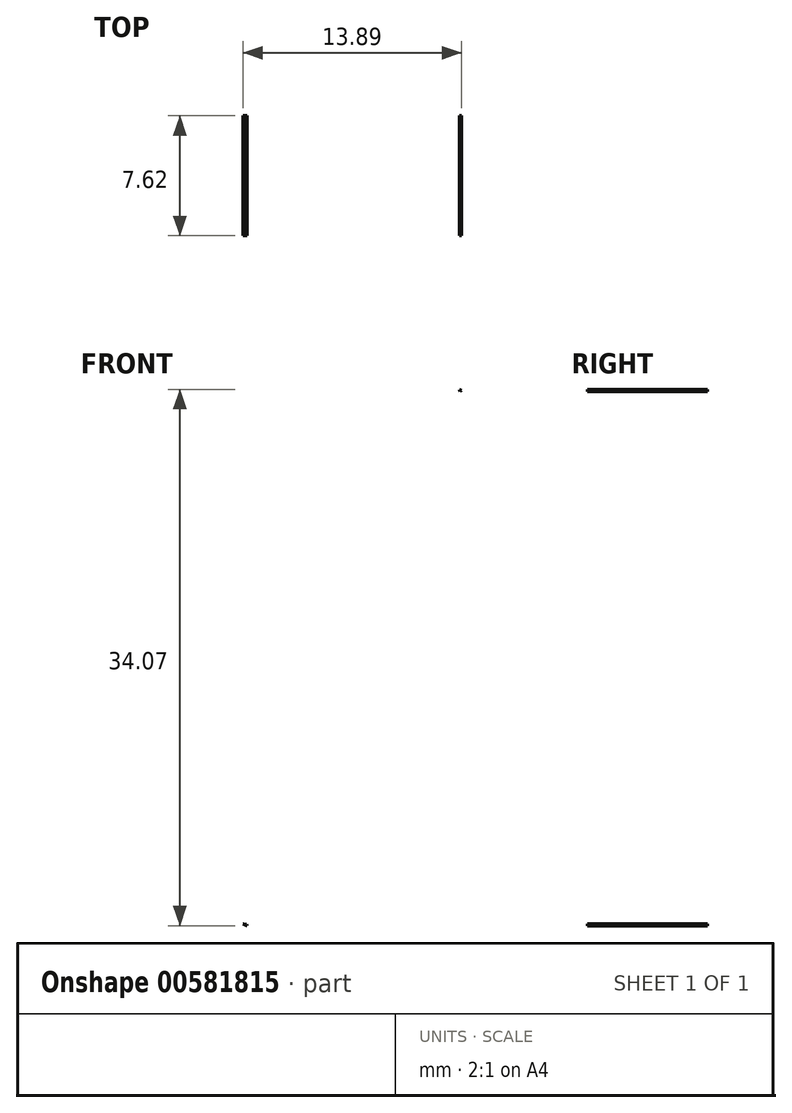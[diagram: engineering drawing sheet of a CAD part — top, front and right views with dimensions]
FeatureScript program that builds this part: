
annotation { "Feature Type Name" : "Feature", "Feature Type Description" : "" }
export const myFeature = defineFeature(function(context is Context, id is Id, definition is map)
    precondition{}
    {
        {
            var Q0;
            Q0=qCreatedBy(makeId("Front.planeOp"),FACE);
            var sketch = newSketch(context, id + "F0", { "sketchPlane" : qUnion([Q0])});
            skLineSegment(sketch, "E0", {"start": v(-52.43, 28.32) * mm, "end": v(-34.99, 41.22) * mm});
            skLineSegment(sketch, "E1", {"start": v(-34.99, 41.22) * mm, "end": v(0, 18.11) * mm});
            skLineSegment(sketch, "E2.MirrorCS", {"start": v(34.99, 41.22) * mm, "end": v(0, 18.11) * mm});
            skLineSegment(sketch, "E3", {"start": v(34.99, 41.22) * mm, "end": v(52.43, 28.32) * mm});
            skLineSegment(sketch, "E4", {"start": v(-52.43, 28.32) * mm, "end": v(-54.84, 6.63) * mm});
            skLineSegment(sketch, "E5.MirrorCS", {"start": v(52.43, 28.32) * mm, "end": v(54.84, 6.63) * mm});
            skLineSegment(sketch, "E6", {"start": v(-54.84, 6.63) * mm, "end": v(-16.04, -8.41) * mm});
            skLineSegment(sketch, "E7.MirrorCS", {"start": v(54.84, 6.63) * mm, "end": v(16.04, -8.41) * mm});
            skLineSegment(sketch, "E8", {"start": v(0, -58.56) * mm, "end": v(19.94, -50.02) * mm});
            skLineSegment(sketch, "E9", {"start": v(19.94, -50.02) * mm, "end": v(16.04, -8.41) * mm});
            skLineSegment(sketch, "E10", {"start": v(0, -58.56) * mm, "end": v(-19.94, -50.02) * mm});
            skLineSegment(sketch, "E11", {"start": v(-19.94, -50.02) * mm, "end": v(-16.04, -8.41) * mm});
            skSolve(sketch);
        }
        {
            var Q0;
            Q0 = qSketchRegion(id + "F0", true);
            extrude(context, id + "F1", {"entities" : qUnion([Q0]), "depth" : 7.62 * mm, "offsetDistance" : 25.4 * mm});
        }
        {
            var Q0;
            Q0=qCreatedBy(makeId("Front.planeOp"),FACE);
            var sketch = newSketch(context, id + "F2", { "sketchPlane" : qUnion([Q0])});
            skCircle(sketch, "E12", {"center": v(0, 0) * mm, "radius": 11 * mm});
            skCircle(sketch, "E13", {"center": v(-33.24, 17) * mm, "radius": 11 * mm});
            skCircle(sketch, "E14", {"center": v(33.05, 17.38) * mm, "radius": 11 * mm});
            skCircle(sketch, "E15", {"center": v(0, -37.34) * mm, "radius": 11 * mm});
            skSolve(sketch);
        }
        {
            var Q0;
            Q0 = qSketchRegion(id + "F2", true);
            extrude(context, id + "F3", {"entities" : qUnion([Q0]), "operationType" : NewBodyOperationType.REMOVE, "endBound" : BoundingType.THROUGH_ALL, "depth" : 25.4 * mm, "offsetDistance" : 25.4 * mm});
        }
        {
            var Q0;
            Q0=qCreatedBy(makeId("Front.planeOp"),FACE);
            var sketch = newSketch(context, id + "F4", { "sketchPlane" : qUnion([Q0])});
            skLineSegment(sketch, "E16", {"start": v(-41.96, 38.65) * mm, "end": v(-26.02, 38.65) * mm});
            skLineSegment(sketch, "E17", {"start": v(-26.02, 38.65) * mm, "end": v(-26.02, 43.76) * mm});
            skLineSegment(sketch, "E18", {"start": v(-26.02, 43.76) * mm, "end": v(-40.46, 43.76) * mm});
            skLineSegment(sketch, "E19", {"start": v(-40.46, 43.76) * mm, "end": v(-41.96, 38.65) * mm});
            skLineSegment(sketch, "E20.MirrorCS", {"start": v(26.02, 43.76) * mm, "end": v(40.46, 43.76) * mm});
            skLineSegment(sketch, "E21.MirrorCS", {"start": v(26.02, 38.65) * mm, "end": v(26.02, 43.76) * mm});
            skLineSegment(sketch, "E22.MirrorCS", {"start": v(41.96, 38.65) * mm, "end": v(26.02, 38.65) * mm});
            skLineSegment(sketch, "E23.MirrorCS", {"start": v(40.46, 43.76) * mm, "end": v(41.96, 38.65) * mm});
            skLineSegment(sketch, "E24", {"start": v(-55.8, 12.48) * mm, "end": v(-47.37, 0) * mm});
            skLineSegment(sketch, "E25", {"start": v(-47.37, 0) * mm, "end": v(-58.2, 0) * mm});
            skLineSegment(sketch, "E26", {"start": v(-58.2, 0) * mm, "end": v(-55.8, 12.48) * mm});
            skLineSegment(sketch, "E27.MirrorCS", {"start": v(55.8, 12.48) * mm, "end": v(47.37, 0) * mm});
            skLineSegment(sketch, "E28.MirrorCS", {"start": v(58.2, 0) * mm, "end": v(55.8, 12.48) * mm});
            skLineSegment(sketch, "E29.MirrorCS", {"start": v(47.37, 0) * mm, "end": v(58.2, 0) * mm});
            skLineSegment(sketch, "E30", {"start": v(-20.6, -44.37) * mm, "end": v(-13.08, -56.1) * mm});
            skLineSegment(sketch, "E31", {"start": v(-13.08, -56.1) * mm, "end": v(-22.1, -56.1) * mm});
            skLineSegment(sketch, "E32", {"start": v(-22.1, -56.1) * mm, "end": v(-20.6, -44.37) * mm});
            skLineSegment(sketch, "E33.MirrorCS", {"start": v(20.6, -44.37) * mm, "end": v(13.08, -56.1) * mm});
            skLineSegment(sketch, "E34.MirrorCS", {"start": v(22.1, -56.1) * mm, "end": v(20.6, -44.37) * mm});
            skLineSegment(sketch, "E35.MirrorCS", {"start": v(13.08, -56.1) * mm, "end": v(22.1, -56.1) * mm});
            skSolve(sketch);
        }
        {
            var Q0;
            Q0 = qSketchRegion(id + "F4", true);
            extrude(context, id + "F5", {"entities" : qUnion([Q0]), "operationType" : NewBodyOperationType.REMOVE, "endBound" : BoundingType.THROUGH_ALL, "depth" : 25.4 * mm, "offsetDistance" : 25.4 * mm});
        }
        {
            var Q0;
            Q0=qCreatedBy(makeId("Front.planeOp"),FACE);
            var sketch = newSketch(context, id + "F6", { "sketchPlane" : qUnion([Q0])});
            skFitSpline(sketch, "E36", {"points": [v(-49.78, 26.92) * mm, v(-44.37, 33.24) * mm, v(-36.85, 36.25) * mm, v(-29.63, 36.25) * mm, v(-24.03, 33.84) * mm, v(-17.6, 27.52) * mm, v(-10.68, 18.2) * mm, v(-4.66, 14.59) * mm, v(0, 13.99) * mm, v(4.96, 14.29) * mm, v(10.68, 17.9) * mm, v(18.2, 27.22) * mm, v(23.91, 34.14) * mm, v(30.23, 36.85) * mm, v(37.75, 36.85) * mm, v(44.97, 32.64) * mm, v(49.78, 26.92) * mm, v(52.49, 19.7) * mm, v(52.49, 11.58) * mm, v(48.88, 5.26) * mm, v(44.97, 2.56) * mm, v(32.03, 0) * mm, v(19.4, -2.26) * mm, v(13.69, -5.26) * mm, v(11.28, -10.38) * mm, v(12.18, -19.1) * mm, v(15.67, -27.22) * mm, v(18.98, -36.85) * mm, v(16.1, -48.88) * mm, v(8.57, -54.6) * mm, v(0, -56.7) * mm, v(-8.27, -54.6) * mm, v(-14.7, -49.78) * mm, v(-18.92, -38.95) * mm, v(-15.6, -25.72) * mm, v(-13.08, -21.5) * mm, v(-13.08, -21.5) * mm, v(-10.68, -15.8) * mm, v(-10.38, -10.08) * mm, v(-15.3, -2.26) * mm, v(-28.84, 0) * mm, v(-37.57, 0) * mm, v(-49.6, 7.07) * mm, v(-52.6, 18.8) * mm, v(-49.78, 26.92) * mm]});
            skLineSegment(sketch, "E37", {"start": v(-24.03, 33.84) * mm, "end": v(9.35, 52.72) * mm});
            skLineSegment(sketch, "E38", {"start": v(9.35, 52.72) * mm, "end": v(23.91, 34.14) * mm});
            skLineSegment(sketch, "E39", {"start": v(-37.57, 0) * mm, "end": v(-18.92, -38.95) * mm});
            skLineSegment(sketch, "E40", {"start": v(18.98, -36.85) * mm, "end": v(44.97, 2.56) * mm});
            skLineSegment(sketch, "E41", {"start": v(-37.57, 0) * mm, "end": v(-62.53, 2.56) * mm});
            skLineSegment(sketch, "E42", {"start": v(-62.53, 2.56) * mm, "end": v(-62.53, 40.46) * mm});
            skLineSegment(sketch, "E43", {"start": v(-62.53, 40.46) * mm, "end": v(-25.53, 49.48) * mm});
            skLineSegment(sketch, "E44", {"start": v(-25.53, 49.48) * mm, "end": v(-24.03, 33.84) * mm});
            skLineSegment(sketch, "E45", {"start": v(23.91, 34.14) * mm, "end": v(37.93, 60.6) * mm});
            skLineSegment(sketch, "E46", {"start": v(37.93, 60.6) * mm, "end": v(59.6, 49.13) * mm});
            skLineSegment(sketch, "E47", {"start": v(59.6, 49.13) * mm, "end": v(65.9, 25.42) * mm});
            skLineSegment(sketch, "E48", {"start": v(65.9, 25.42) * mm, "end": v(57.48, -5.56) * mm});
            skLineSegment(sketch, "E49", {"start": v(57.48, -5.56) * mm, "end": v(44.97, 2.56) * mm});
            skLineSegment(sketch, "E50", {"start": v(18.98, -36.85) * mm, "end": v(30.41, -52.79) * mm});
            skLineSegment(sketch, "E51", {"start": v(30.41, -52.79) * mm, "end": v(0, -70) * mm});
            skLineSegment(sketch, "E52", {"start": v(0, -70) * mm, "end": v(-28.54, -58.5) * mm});
            skLineSegment(sketch, "E53", {"start": v(-28.54, -58.5) * mm, "end": v(-18.92, -38.95) * mm});
            skSolve(sketch);
        }
        {
            var Q0;
            {var subQ0=sQuery(id+"F6.wireOp",EDGE,"E37");Q0=makeQuery(id+"F6.imprint","IMPRINT",FACE,{"disambiguationData":[TD([[makeQuery(id+"F6.imprint","IMPRINT",EDGE,{"derivedFrom":subQ0}),-1.0]])]});}
            var Q1;
            {var subQ0=sQuery(id+"F6.wireOp",EDGE,"E45");Q1=makeQuery(id+"F6.imprint","IMPRINT",FACE,{"disambiguationData":[TD([[makeQuery(id+"F6.imprint","IMPRINT",EDGE,{"derivedFrom":subQ0}),-1.0]])]});}
            var Q2;
            {var subQ0=sQuery(id+"F6.wireOp",EDGE,"E40");Q2=makeQuery(id+"F6.imprint","IMPRINT",FACE,{"disambiguationData":[TD([[makeQuery(id+"F6.imprint","IMPRINT",EDGE,{"derivedFrom":subQ0}),1.0]])]});}
            var Q3;
            {var subQ0=sQuery(id+"F6.wireOp",EDGE,"E50");Q3=makeQuery(id+"F6.imprint","IMPRINT",FACE,{"disambiguationData":[TD([[makeQuery(id+"F6.imprint","IMPRINT",EDGE,{"derivedFrom":subQ0}),-1.0]])]});}
            var Q4;
            {var subQ0=sQuery(id+"F6.wireOp",EDGE,"E39");Q4=makeQuery(id+"F6.imprint","IMPRINT",FACE,{"disambiguationData":[TD([[makeQuery(id+"F6.imprint","IMPRINT",EDGE,{"derivedFrom":subQ0}),1.0]])]});}
            var Q5;
            {var subQ0=sQuery(id+"F6.wireOp",EDGE,"E41");Q5=makeQuery(id+"F6.imprint","IMPRINT",FACE,{"disambiguationData":[TD([[makeQuery(id+"F6.imprint","IMPRINT",EDGE,{"derivedFrom":subQ0}),-1.0]])]});}
            extrude(context, id + "F7", {"entities" : qUnion([Q0, Q1, Q2, Q3, Q4, Q5]), "operationType" : NewBodyOperationType.REMOVE, "endBound" : BoundingType.THROUGH_ALL, "depth" : 25.4 * mm, "offsetDistance" : 25.4 * mm});
        }
        {
            var Q0;
            Q0=qCreatedBy(makeId("Front.planeOp"),FACE);
            var sketch = newSketch(context, id + "F8", { "sketchPlane" : qUnion([Q0])});
            skLineSegment(sketch, "E54", {"start": v(16.28, -23.91) * mm, "end": v(19.28, -36.25) * mm});
            skLineSegment(sketch, "E55", {"start": v(19.28, -36.25) * mm, "end": v(19.28, -30.08) * mm});
            skPoint(sketch, "E55.endSnap0", {"position": v(17.78, -30.08) * mm});
            skLineSegment(sketch, "E56", {"start": v(19.28, -30.08) * mm, "end": v(16.28, -23.91) * mm});
            skSolve(sketch);
        }
        {
            var Q0;
            Q0 = qSketchRegion(id + "F8", true);
            extrude(context, id + "F9", {"entities" : qUnion([Q0]), "operationType" : NewBodyOperationType.REMOVE, "depth" : 25.4 * mm, "offsetDistance" : 25.4 * mm});
        }
    });
